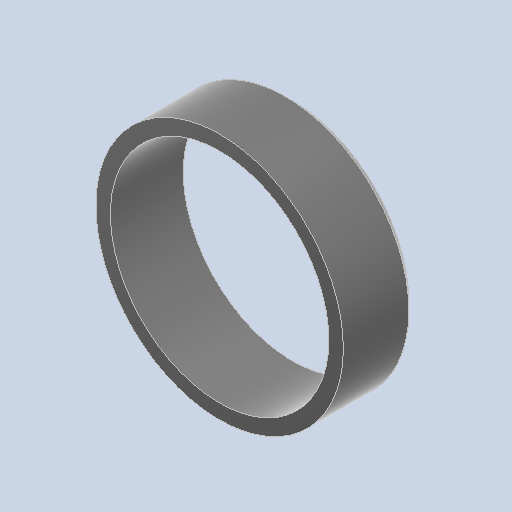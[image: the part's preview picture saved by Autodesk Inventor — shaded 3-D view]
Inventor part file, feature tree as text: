
AUTODESK INVENTOR PART (.ipt)
format: ipt  version: 2023 (Build 270158030, 158C)  size: 113,664 bytes
history: native  units: mm
features: extrude x1, chamfer x1, sketch x1
ambient origin geometry x8: Origin, YZ Plane, XZ Plane, XY Plane, X Axis, Y Axis, Z Axis, Center Point
bodies: Solid1 (feature_tree)
feature tree (3):
  extrude  "Extrusion1"  Depth=5.0mm
  chamfer  "Chamfer1"  Distance=5.0mm
  sketch  "Sketch1"  dims[d0=15.0mm d1=17.0mm d2=5.0mm d3=0.0mm d4=0.5mm d5=2.0mm d6=45.0deg]
